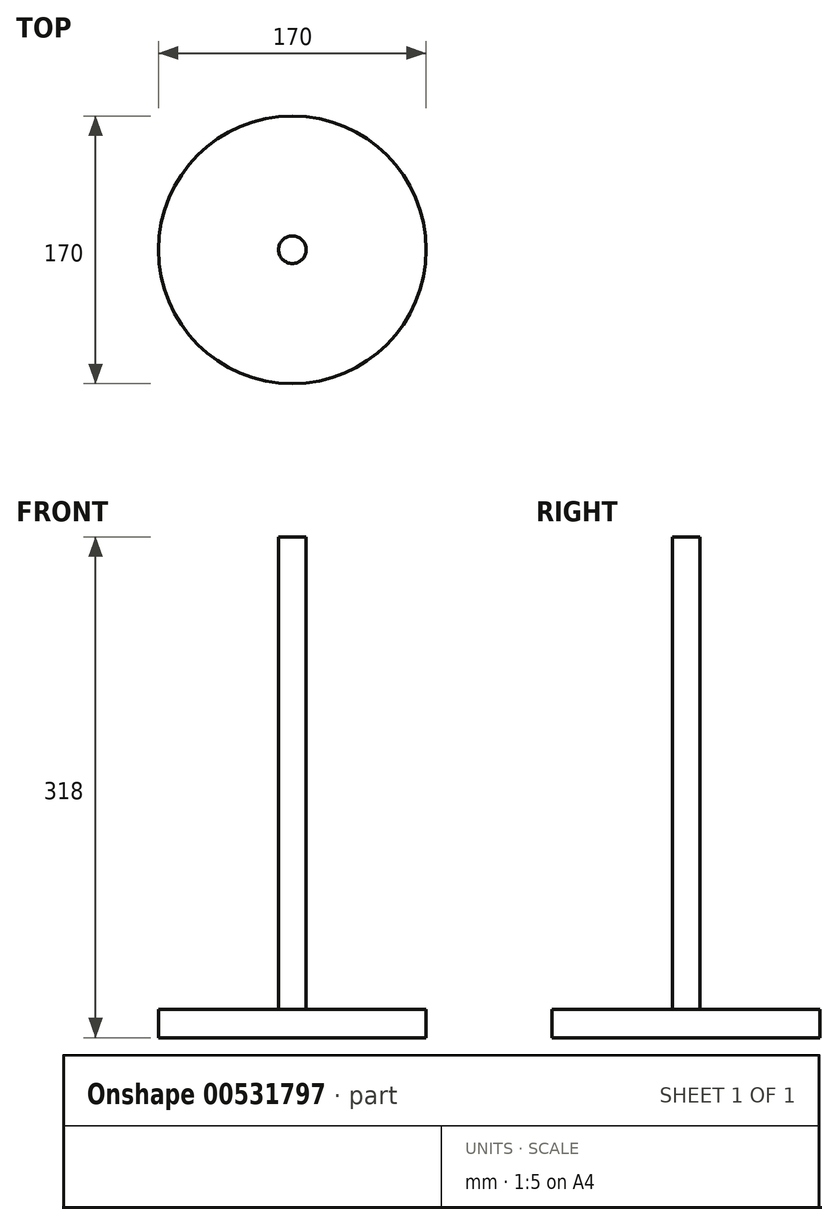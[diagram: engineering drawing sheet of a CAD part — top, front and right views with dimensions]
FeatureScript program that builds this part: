
annotation { "Feature Type Name" : "Feature", "Feature Type Description" : "" }
export const myFeature = defineFeature(function(context is Context, id is Id, definition is map)
    precondition{}
    {
        {
            var Q0;
            Q0=qCreatedBy(makeId("Top.planeOp"),FACE);
            var sketch = newSketch(context, id + "F0", { "sketchPlane" : qUnion([Q0])});
            skPoint(sketch, "E0.middle", {"position": v(0, 0) * mm});
            skCircle(sketch, "E1", {"center": v(0, 0) * mm, "radius": 85 * mm});
            skPoint(sketch, "E2.orphan", {"position": v(-85, 85) * mm});
            skPoint(sketch, "E3.orphan", {"position": v(85, 85) * mm});
            skPoint(sketch, "E4.orphan", {"position": v(85, -85) * mm});
            skPoint(sketch, "E0.right.end.orphan", {"position": v(-85, -85) * mm});
            skSolve(sketch);
        }
        {
            var Q0;
            Q0 = qSketchRegion(id + "F0", true);
            extrude(context, id + "F1", {"entities" : qUnion([Q0]), "depth" : 18 * mm, "offsetDistance" : 25 * mm});
        }
        {
            var Q0;
            Q0=makeQuery(id+"F1.opExtrude","CAP_FACE",FACE,{"disambiguationData":[OSD([sQuery(id+"F0.wireOp",EDGE,"E1")])],"isStart":false});
            var sketch = newSketch(context, id + "F2", { "sketchPlane" : qUnion([Q0])});
            skCircle(sketch, "E5", {"center": v(0, 0) * mm, "radius": 8.75 * mm});
            skSolve(sketch);
        }
        {
            var Q0;
            Q0 = qSketchRegion(id + "F2", true);
            extrude(context, id + "F3", {"entities" : qUnion([Q0]), "operationType" : NewBodyOperationType.ADD, "depth" : 300 * mm, "offsetDistance" : 25 * mm});
        }
    });
